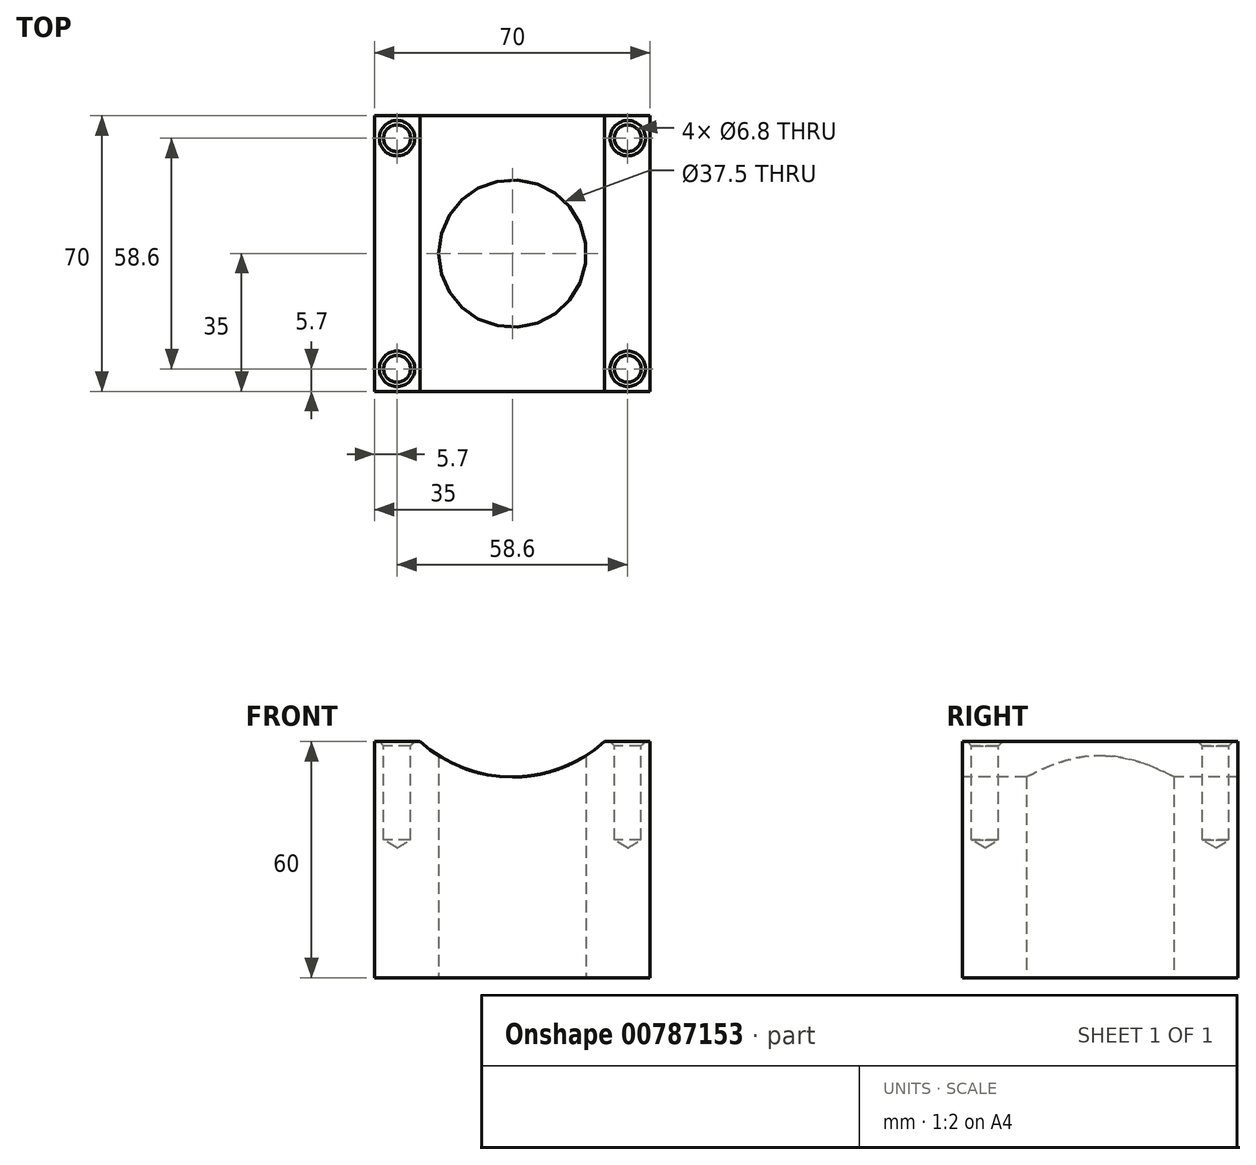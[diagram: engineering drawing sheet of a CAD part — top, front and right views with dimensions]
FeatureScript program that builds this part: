
annotation { "Feature Type Name" : "Feature", "Feature Type Description" : "" }
export const myFeature = defineFeature(function(context is Context, id is Id, definition is map)
    precondition{}
    {
        {
            var Q0;
            Q0=qCreatedBy(makeId("Top.planeOp"),FACE);
            var sketch = newSketch(context, id + "F0", { "sketchPlane" : qUnion([Q0])});
            skLineSegment(sketch, "E0.bottom", {"start": v(-35, 35) * mm, "end": v(35, 35) * mm});
            skLineSegment(sketch, "E0.top", {"start": v(-35, -35) * mm, "end": v(35, -35) * mm});
            skLineSegment(sketch, "E0.left", {"start": v(-35, 35) * mm, "end": v(-35, -35) * mm});
            skLineSegment(sketch, "E0.right", {"start": v(35, 35) * mm, "end": v(35, -35) * mm});
            skPoint(sketch, "E0.middle", {"position": v(0, 0) * mm});
            skCircle(sketch, "E1", {"center": v(0, 0) * mm, "radius": 18.75 * mm});
            skSolve(sketch);
        }
        {
            var Q0;
            Q0 = qSketchRegion(id + "F0", true);
            var Q1;
            Q1=makeQuery(id+"F0.imprint","IMPRINT",FACE,{"disambiguationData":[TD([[makeQuery(id+"F0.imprint","IMPRINT",EDGE,{"derivedFrom":sQuery(id+"F0.wireOp",EDGE,"E0.bottom")}),-1.0]])]});
            extrude(context, id + "F1", {"entities" : qUnion([Q0, Q1]), "depth" : 60 * mm, "offsetDistance" : 25 * mm});
        }
        {
            var Q0;
            Q0=qCreatedBy(makeId("Front.planeOp"),FACE);
            var sketch = newSketch(context, id + "F2", { "sketchPlane" : qUnion([Q0])});
            skCircle(sketch, "E2", {"center": v(0, 86) * mm, "radius": 35 * mm});
            skSolve(sketch);
        }
        {
            var Q0;
            Q0 = qSketchRegion(id + "F2", true);
            extrude(context, id + "F3", {"entities" : qUnion([Q0]), "operationType" : NewBodyOperationType.REMOVE, "endBound" : BoundingType.THROUGH_ALL, "oppositeDirection" : true, "depth" : 25 * mm, "offsetDistance" : 25 * mm, "hasSecondDirection" : true, "secondDirectionBound" : SecondDirectionBoundingType.THROUGH_ALL, "secondDirectionOppositeDirection" : false, "secondDirectionDepth" : 25 * mm});
        }
        {
            var Q0;
            {var subQ0=sQuery(id+"F0.wireOp",EDGE,"E0.bottom");var subQ1=makeQuery(id+"F1.opExtrude","SWEPT_FACE",FACE,{"disambiguationData":[OSD([subQ0])]});var subQ3=sQuery(id+"F0.wireOp",EDGE,"E0.left");var subQ4=makeQuery(id+"F1.opExtrude","SWEPT_FACE",FACE,{"disambiguationData":[OSD([subQ3])]});var subQ6=sQuery(id+"F0.wireOp",EDGE,"E0.top");Q0=makeQuery(id+"FPudWfUKxNzHFPY_1.1.F3.boolean.opBoolean","SPLIT",FACE,{"disambiguationData":[TD([subQ1])],"derivedFrom":makeQuery(id+"F3.boolean.opBoolean","SPLIT",FACE,{"disambiguationData":[TD([subQ4])],"derivedFrom":makeQuery(id+"F1.opExtrude","CAP_FACE",FACE,{"disambiguationData":[OSD([subQ0,subQ6,subQ3,sQuery(id+"F0.wireOp",EDGE,"E0.right"),sQuery(id+"F0.wireOp",EDGE,"E1")])],"isStart":false})})});}
            var sketch = newSketch(context, id + "F4", { "sketchPlane" : qUnion([Q0])});
            skLineSegment(sketch, "E3.bottom", {"start": v(-29.3, 29.3) * mm, "end": v(29.3, 29.3) * mm});
            skLineSegment(sketch, "E3.top", {"start": v(-29.3, -29.3) * mm, "end": v(29.3, -29.3) * mm});
            skLineSegment(sketch, "E3.left", {"start": v(-29.3, 29.3) * mm, "end": v(-29.3, -29.3) * mm});
            skLineSegment(sketch, "E3.right", {"start": v(29.3, 29.3) * mm, "end": v(29.3, -29.3) * mm});
            skPoint(sketch, "E3.middle", {"position": v(0, 0) * mm});
            skSolve(sketch);
        }
        {
            var Q0;
            Q0=sQuery(id+"F4.wireOp",VERTEX,"E3.bottom.start");
            var Q1;
            Q1=sQuery(id+"F4.wireOp",VERTEX,"E3.bottom.end");
            var Q2;
            Q2=sQuery(id+"F4.wireOp",VERTEX,"E3.top.end");
            var Q3;
            Q3=sQuery(id+"F4.wireOp",VERTEX,"E3.top.start");
            var Q4;
            Q4=makeQuery(id+"F1.opExtrude","SWEPT_BODY",BODY,{"disambiguationData":[OSD([sQuery(id+"F0.wireOp",EDGE,"E0.bottom"),sQuery(id+"F0.wireOp",EDGE,"E0.top"),sQuery(id+"F0.wireOp",EDGE,"E0.left"),sQuery(id+"F0.wireOp",EDGE,"E0.right"),sQuery(id+"F0.wireOp",EDGE,"E1")])]});
            hole(context, id + "F5", {"style" : HoleStyle.C_SINK, "endStyle" : HoleEndStyle.BLIND, "holeDiameter" : 6.8 * mm, "cSinkDiameter" : 9 * mm, "cSinkAngle" : 90 * degree, "majorDiameter" : 5 * mm, "holeDepth" : 25 * mm, "isTappedThrough" : true, "tappedDepth" : 12 * mm, "tapClearance" : 3, "locations" : qUnion([Q0, Q1, Q2, Q3]), "scope" : qUnion([Q4])});
        }
    });
